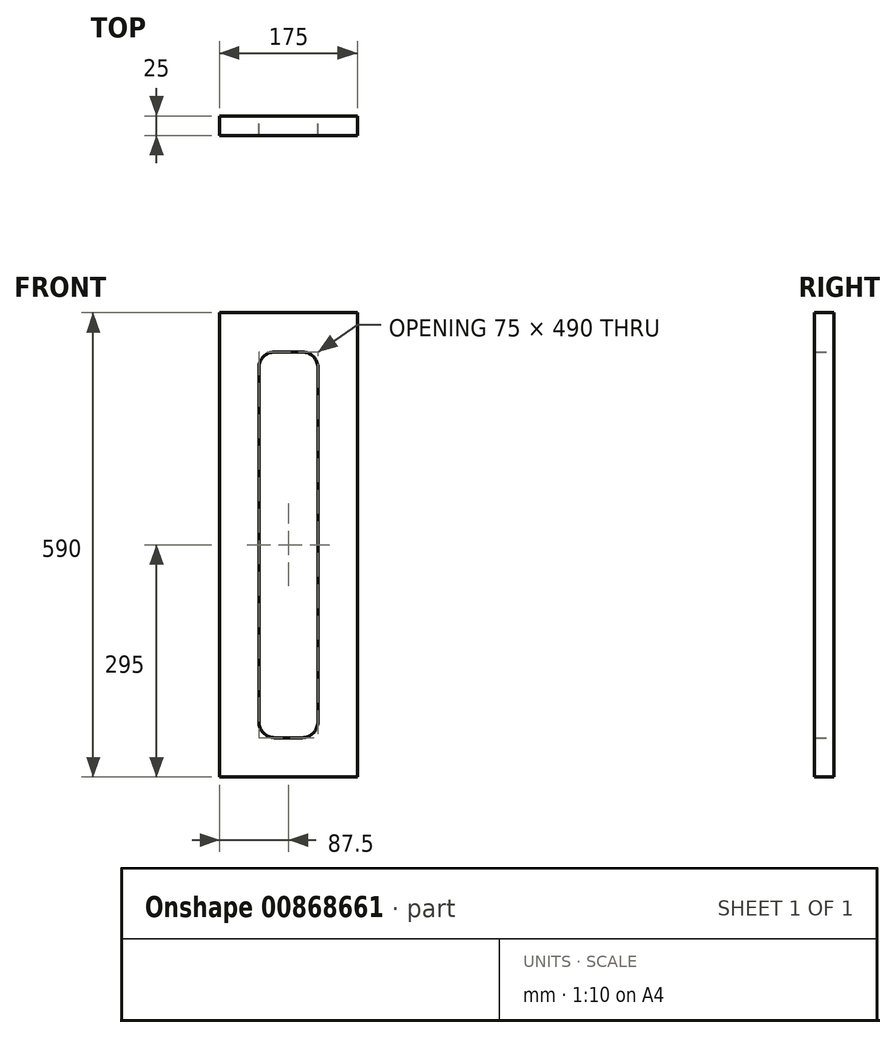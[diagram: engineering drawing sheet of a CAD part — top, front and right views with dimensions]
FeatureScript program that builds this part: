
annotation { "Feature Type Name" : "Feature", "Feature Type Description" : "" }
export const myFeature = defineFeature(function(context is Context, id is Id, definition is map)
    precondition{}
    {
        {
            var Q0;
            Q0=qCreatedBy(makeId("Front.planeOp"),FACE);
            var sketch = newSketch(context, id + "F0", { "sketchPlane" : qUnion([Q0])});
            skLineSegment(sketch, "E0.bottom", {"start": v(-87.5, 295) * mm, "end": v(87.5, 295) * mm});
            skLineSegment(sketch, "E0.top", {"start": v(-87.5, -295) * mm, "end": v(87.5, -295) * mm});
            skLineSegment(sketch, "E0.left", {"start": v(-87.5, 295) * mm, "end": v(-87.5, -295) * mm});
            skLineSegment(sketch, "E0.right", {"start": v(87.5, 295) * mm, "end": v(87.5, -295) * mm});
            skPoint(sketch, "E0.middle", {"position": v(0, 0) * mm});
            skLineSegment(sketch, "E1.bottom", {"start": v(-17.5, 245) * mm, "end": v(17.5, 245) * mm});
            skLineSegment(sketch, "E1.top", {"start": v(-17.5, -245) * mm, "end": v(17.5, -245) * mm});
            skLineSegment(sketch, "E1.left", {"start": v(-37.5, 225) * mm, "end": v(-37.5, -225) * mm});
            skPoint(sketch, "E2.visualSharp", {"position": v(-37.5, 245) * mm});
            skArc(sketch, "E2.filletArc", {"start": v(-17.5, 245) * mm, "mid": v(-31.64, 239.14) * mm, "end": v(-37.5, 225) * mm});
            skPoint(sketch, "E3.visualSharp", {"position": v(37.5, 245) * mm});
            skArc(sketch, "E3.filletArc", {"start": v(37.5, 225) * mm, "mid": v(31.64, 239.14) * mm, "end": v(17.5, 245) * mm});
            skPoint(sketch, "E4.visualSharp", {"position": v(-37.5, -245) * mm});
            skArc(sketch, "E4.filletArc", {"start": v(-37.5, -225) * mm, "mid": v(-31.64, -239.14) * mm, "end": v(-17.5, -245) * mm});
            skLineSegment(sketch, "E5", {"start": v(37.5, 225) * mm, "end": v(37.5, -225) * mm});
            skPoint(sketch, "E6.visualSharp", {"position": v(37.5, -245) * mm});
            skArc(sketch, "E6.filletArc", {"start": v(17.5, -245) * mm, "mid": v(31.64, -239.14) * mm, "end": v(37.5, -225) * mm});
            skSolve(sketch);
        }
        {
            var Q0;
            Q0=makeQuery(id+"F0.imprint","IMPRINT",FACE,{"disambiguationData":[TD([[makeQuery(id+"F0.imprint","IMPRINT",EDGE,{"derivedFrom":sQuery(id+"F0.wireOp",EDGE,"E0.bottom")}),-1.0]])]});
            extrude(context, id + "F1", {"entities" : qUnion([Q0]), "depth" : 25 * mm, "offsetDistance" : 25 * mm});
        }
    });
